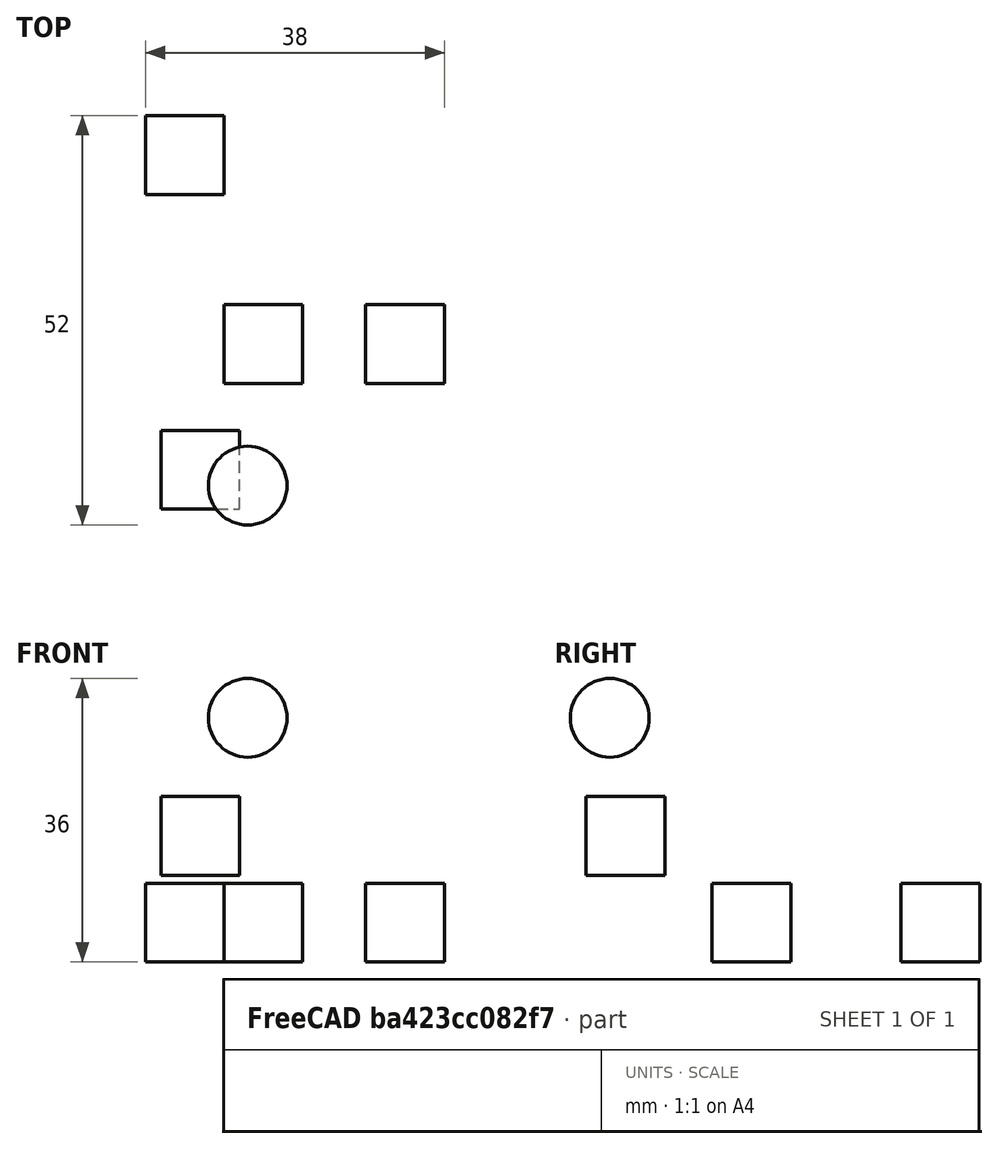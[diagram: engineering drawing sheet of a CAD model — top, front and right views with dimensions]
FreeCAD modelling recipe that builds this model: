
FCSTD DOCUMENT  (FreeCAD 0.18.1R)
Label: sub_b
License: All rights reserved
LicenseURL: http://en.wikipedia.org/wiki/All_rights_reserved
objects: Part::Box×4, Part::Sphere×1
note: 5 computed .brp shape members not serialized (recipe doc carries the construction recipe); baked Part::Feature solids carry a one-line shape summary decoded from their .brp

FEATURE [Part::Box] Box  label="Cube"
  AttacherType = Attacher::AttachEngine3D
  Height = 10
  Length = 10
  Placement = pos=(8,24,0) rot=(0,0,1;0rad)
  Width = 10
FEATURE [Part::Box] Box001  label="Cube001"
  AttacherType = Attacher::AttachEngine3D
  Height = 10
  Length = 10
  Placement = pos=(18,0,0) rot=(0,0,1;0rad)
  Width = 10
FEATURE [Part::Box] Box002  label="Cube002"
  AttacherType = Attacher::AttachEngine3D
  Height = 10
  Length = 10
  Placement = pos=(36,0,0) rot=(0,0,1;0rad)
  Width = 10
FEATURE [Part::Box] Box003  label="Cube003"
  AttacherType = Attacher::AttachEngine3D
  Height = 10
  Length = 10
  Placement = pos=(10,-16,11) rot=(0,0,1;0rad)
  Width = 10
FEATURE [Part::Sphere] Sphere
  Angle1 = -90
  Angle2 = 90
  Angle3 = 360
  AttacherType = Attacher::AttachEngine3D
  Placement = pos=(21,-13,31) rot=(0,0,1;0rad)
  Radius = 5
